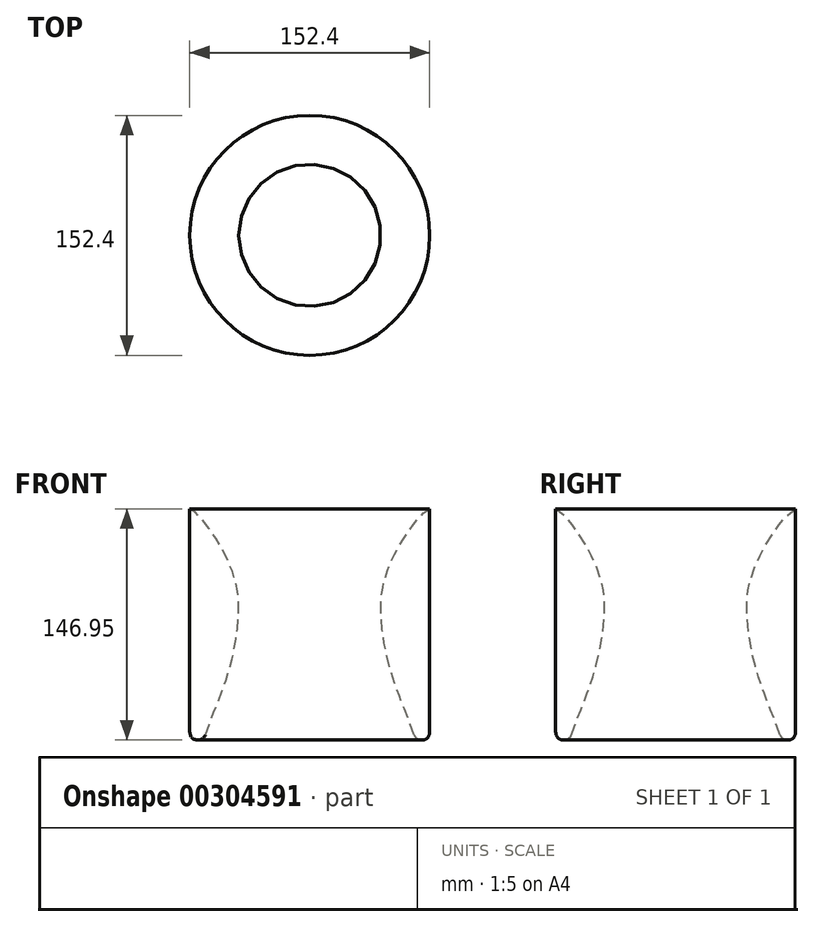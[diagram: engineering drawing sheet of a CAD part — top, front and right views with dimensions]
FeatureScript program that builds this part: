
annotation { "Feature Type Name" : "Feature", "Feature Type Description" : "" }
export const myFeature = defineFeature(function(context is Context, id is Id, definition is map)
    precondition{}
    {
        {
            var Q0;
            Q0=qCreatedBy(makeId("Front.planeOp"),FACE);
            var sketch = newSketch(context, id + "F0", { "sketchPlane" : qUnion([Q0])});
            skLineSegment(sketch, "E0.bottom", {"start": v(0, 0) * mm, "end": v(-76.2, 0) * mm});
            skLineSegment(sketch, "E0.top", {"start": v(0, 304.8) * mm, "end": v(-76.2, 304.8) * mm});
            skLineSegment(sketch, "E0.left", {"start": v(0, 0) * mm, "end": v(0, 304.8) * mm});
            skLineSegment(sketch, "E0.right", {"start": v(-76.2, 0) * mm, "end": v(-76.2, 304.8) * mm});
            skFitSpline(sketch, "E1", {"points": [v(0, 0) * mm, v(-66.7, 4.16) * mm, v(-70.34, 14.61) * mm, v(-76.2, 86.35) * mm, v(-70.62, 147.73) * mm, v(-53.34, 195.64) * mm, v(-45.4, 234.53) * mm, v(-51.05, 269.75) * mm, v(-76.2, 304.8) * mm], "startDerivative": vector(-1190.49, 0) * mm, "endDerivative": vector(-168.25, 75.16) * mm});
            skFitSpline(sketch, "E2.0", {"points": [v(0, 1.02) * mm, v(-12.4, 1.02) * mm, v(-27.39, 0.97) * mm, v(-41.61, 0.99) * mm, v(-49.77, 1.08) * mm, v(-55.77, 1.28) * mm, v(-59.97, 1.65) * mm, v(-62.25, 2.1) * mm, v(-63.5, 2.55) * mm, v(-64.2, 2.92) * mm, v(-64.75, 3.33) * mm, v(-65.21, 3.8) * mm, v(-65.65, 4.39) * mm, v(-66.1, 5.1) * mm, v(-66.54, 5.9) * mm, v(-67.13, 7.13) * mm, v(-67.88, 9.02) * mm, v(-68.61, 11.56) * mm, v(-69.19, 14.05) * mm, v(-69.62, 16.17) * mm, v(-70.04, 18.55) * mm, v(-70.6, 22.03) * mm, v(-71.26, 26.9) * mm, v(-72, 33.49) * mm, v(-72.94, 43.03) * mm, v(-73.73, 53.47) * mm, v(-74.37, 64.25) * mm, v(-74.76, 72.38) * mm, v(-75, 79.07) * mm, v(-75.14, 84.3) * mm, v(-75.25, 89.44) * mm, v(-75.3, 95.64) * mm, v(-75.23, 105.18) * mm, v(-74.77, 116.4) * mm, v(-73.71, 126.93) * mm, v(-72.45, 135.04) * mm, v(-71.27, 141) * mm, v(-69.85, 146.86) * mm, v(-68.17, 152.67) * mm, v(-66.27, 158.43) * mm, v(-63.53, 166.05) * mm, v(-59.84, 175.46) * mm, v(-56.17, 184.73) * mm, v(-53.46, 192.08) * mm, v(-51.61, 197.55) * mm, v(-49.98, 202.98) * mm, v(-48.07, 210.14) * mm, v(-46.57, 217.17) * mm, v(-45.46, 224.04) * mm, v(-44.83, 229.1) * mm, v(-44.38, 234.06) * mm, v(-44.13, 238.91) * mm, v(-44.1, 243.73) * mm, v(-44.48, 250.16) * mm, v(-45.55, 256.72) * mm, v(-47.56, 263.64) * mm, v(-49.24, 268.15) * mm, v(-50.88, 271.9) * mm, v(-52.69, 275.73) * mm, v(-55.24, 280.6) * mm, v(-58.63, 286.33) * mm, v(-62.21, 291.74) * mm, v(-65.84, 296.62) * mm, v(-69.4, 300.75) * mm, v(-72.18, 303.4) * mm, v(-74.28, 304.94) * mm, v(-75.29, 305.5) * mm, v(-75.79, 305.73) * mm]});
            skLineSegment(sketch, "E3", {"start": v(-76.2, 304.8) * mm, "end": v(-66, 304.8) * mm});
            skSolve(sketch);
        }
        {
            var Q0;
            {var subQ0=sQuery(id+"F0.wireOp",EDGE,"E1");var subQ3=sQuery(id+"F0.wireOp",EDGE,"E0.right");var subQ4=makeQuery(id+"F0.imprint","INTERSECT",VERTEX,{"disambiguationData":[OD(0.0)],"derivedFrom":[subQ3,subQ0]});Q0=makeQuery(id+"F0.imprint","IMPRINT",FACE,{"disambiguationData":[TD([[makeQuery(id+"F0.imprint","IMPRINT",EDGE,{"disambiguationData":[TD([[subQ4,-1.0]])],"derivedFrom":subQ3}),-1.0]])]});}
            var Q1;
            Q1=sQuery(id+"F0.wireOp",EDGE,"E0.left");
            revolve(context, id + "F1", {"entities" : qUnion([Q0]), "axis" : qUnion([Q1]), "revolveType" : RevolveType.FULL});
        }
        {
            var Q0;
            Q0=makeQuery(id+"F1.opRevolve","SWEPT_EDGE",EDGE,{"disambiguationData":[OSD([sQuery(id+"F0.wireOp",EDGE,"E0.right"),sQuery(id+"F0.wireOp",EDGE,"E1"),sQuery(id+"F0.wireOp",EDGE,"E3")])]});
            fillet(context, id + "F2", {"entities" : qUnion([Q0]), "radius" : 5.08 * mm, "tangentPropagation" : true, "allowEdgeOverflow" : false});
        }
    });
